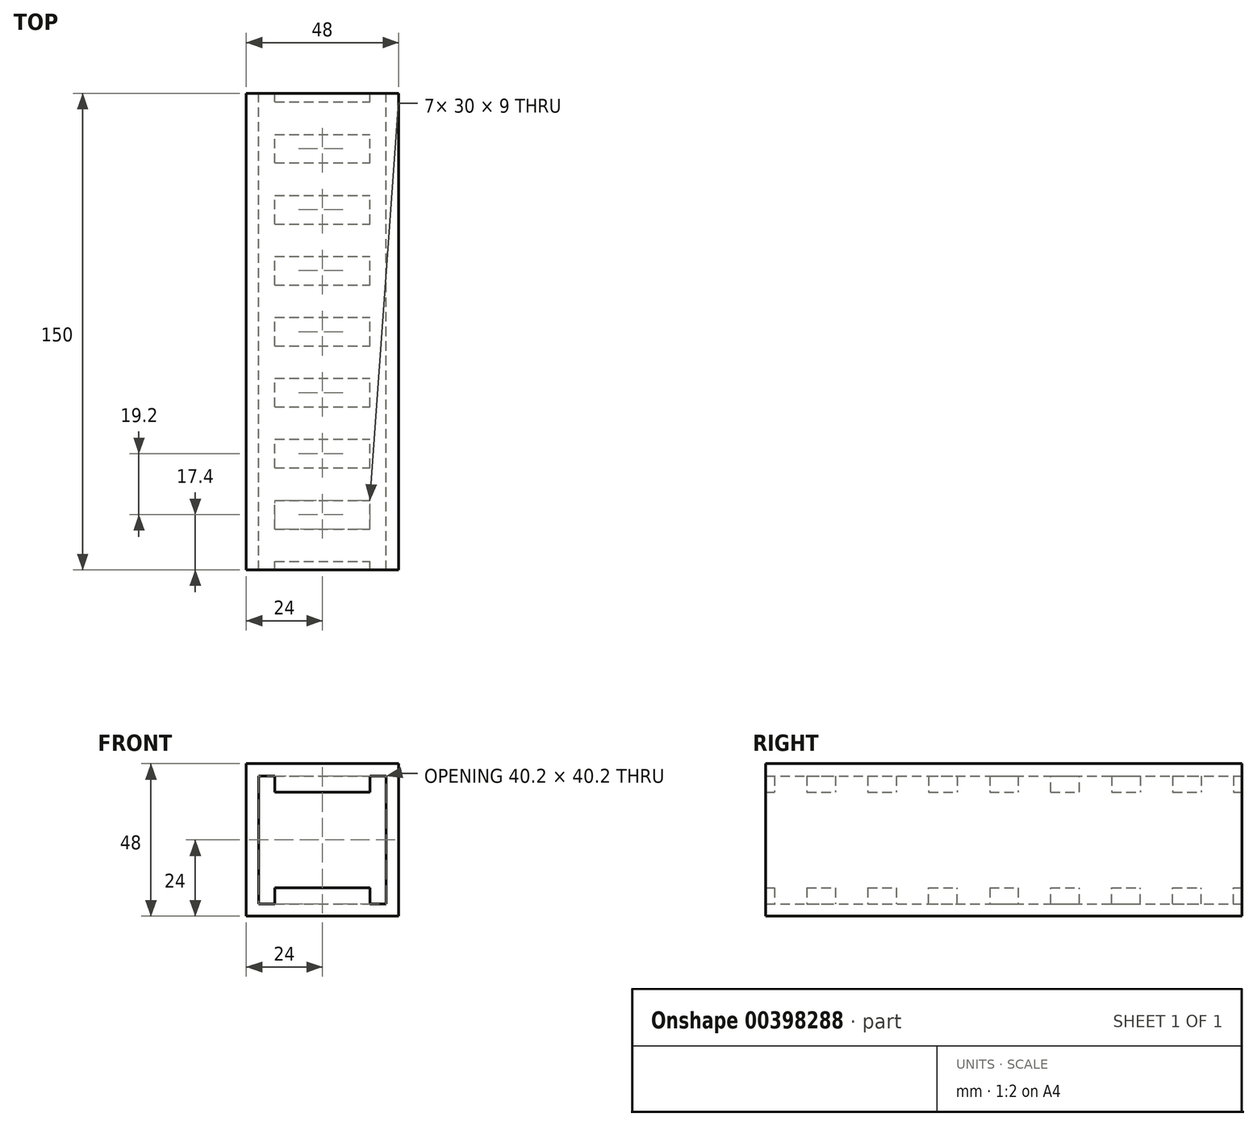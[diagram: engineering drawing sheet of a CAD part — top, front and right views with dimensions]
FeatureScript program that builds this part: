
annotation { "Feature Type Name" : "Feature", "Feature Type Description" : "" }
export const myFeature = defineFeature(function(context is Context, id is Id, definition is map)
    precondition{}
    {
        {
            var Q0;
            Q0=qCreatedBy(makeId("Front.planeOp"),FACE);
            var sketch = newSketch(context, id + "F0", { "sketchPlane" : qUnion([Q0])});
            skLineSegment(sketch, "E0.bottom", {"start": v(-24, 24) * mm, "end": v(24, 24) * mm});
            skLineSegment(sketch, "E0.top", {"start": v(-24, -24) * mm, "end": v(24, -24) * mm});
            skLineSegment(sketch, "E0.left", {"start": v(-24, 24) * mm, "end": v(-24, -24) * mm});
            skLineSegment(sketch, "E0.right", {"start": v(24, 24) * mm, "end": v(24, -24) * mm});
            skPoint(sketch, "E0.middle", {"position": v(0, 0) * mm});
            skLineSegment(sketch, "E1.bottom", {"start": v(20.1, 20.1) * mm, "end": v(-20.1, 20.1) * mm});
            skLineSegment(sketch, "E1.top", {"start": v(20.1, -20.1) * mm, "end": v(-20.1, -20.1) * mm});
            skLineSegment(sketch, "E1.left", {"start": v(20.1, 20.1) * mm, "end": v(20.1, -20.1) * mm});
            skLineSegment(sketch, "E1.right", {"start": v(-20.1, 20.1) * mm, "end": v(-20.1, -20.1) * mm});
            skSolve(sketch);
        }
        {
            var Q0;
            Q0 = qSketchRegion(id + "F0", true);
            extrude(context, id + "F1", {"entities" : qUnion([Q0]), "depth" : 150 * mm});
        }
        {
            var Q0;
            Q0=qCreatedBy(makeId("Front.planeOp"),FACE);
            var sketch = newSketch(context, id + "F2", { "sketchPlane" : qUnion([Q0])});
            skLineSegment(sketch, "E2.bottom", {"start": v(-15, 20.1) * mm, "end": v(15, 20.1) * mm});
            skLineSegment(sketch, "E2.top", {"start": v(-15, 15.1) * mm, "end": v(15, 15.1) * mm});
            skLineSegment(sketch, "E2.left", {"start": v(-15, 20.1) * mm, "end": v(-15, 15.1) * mm});
            skLineSegment(sketch, "E2.right", {"start": v(15, 20.1) * mm, "end": v(15, 15.1) * mm});
            skLineSegment(sketch, "E3.bottom", {"start": v(-15, -20.1) * mm, "end": v(15, -20.1) * mm});
            skLineSegment(sketch, "E3.top", {"start": v(-15, -15.1) * mm, "end": v(15, -15.1) * mm});
            skLineSegment(sketch, "E3.left", {"start": v(-15, -20.1) * mm, "end": v(-15, -15.1) * mm});
            skLineSegment(sketch, "E3.right", {"start": v(15, -20.1) * mm, "end": v(15, -15.1) * mm});
            skSolve(sketch);
        }
        {
            var Q0;
            Q0 = qSketchRegion(id + "F2", true);
            extrude(context, id + "F3", {"entities" : qUnion([Q0]), "operationType" : NewBodyOperationType.ADD, "depth" : 2.7 * mm});
        }
        {
            var Q0;
            Q0=qCreatedBy(makeId("Front.planeOp"),FACE);
            cPlane(context, id + "F4", {"entities" : qUnion([Q0]), "cplaneType" : CPlaneType.OFFSET, "offset" : 12.9 * mm, "width" : 150 * mm, "height" : 150 * mm});
        }
        {
            var Q0;
            Q0=qCreatedBy(id+"F4.planeOp",FACE);
            var sketch = newSketch(context, id + "F5", { "sketchPlane" : qUnion([Q0])});
            skLineSegment(sketch, "E4.bottom", {"start": v(-15, 20.1) * mm, "end": v(15, 20.1) * mm});
            skLineSegment(sketch, "E4.top", {"start": v(-15, 15.1) * mm, "end": v(15, 15.1) * mm});
            skLineSegment(sketch, "E4.left", {"start": v(-15, 20.1) * mm, "end": v(-15, 15.1) * mm});
            skLineSegment(sketch, "E4.right", {"start": v(15, 20.1) * mm, "end": v(15, 15.1) * mm});
            skLineSegment(sketch, "E5.bottom", {"start": v(-15, -20.1) * mm, "end": v(15, -20.1) * mm});
            skLineSegment(sketch, "E5.top", {"start": v(-15, -15.1) * mm, "end": v(15, -15.1) * mm});
            skLineSegment(sketch, "E5.left", {"start": v(-15, -20.1) * mm, "end": v(-15, -15.1) * mm});
            skLineSegment(sketch, "E5.right", {"start": v(15, -20.1) * mm, "end": v(15, -15.1) * mm});
            skSolve(sketch);
        }
        {
            var Q0;
            Q0 = qSketchRegion(id + "F5", true);
            extrude(context, id + "F6", {"entities" : qUnion([Q0]), "operationType" : NewBodyOperationType.ADD, "depth" : 9 * mm});
        }
        {
            var Q0;
            Q0=qCreatedBy(makeId("Front.planeOp"),FACE);
            cPlane(context, id + "F7", {"entities" : qUnion([Q0]), "cplaneType" : CPlaneType.OFFSET, "offset" : 32.1 * mm, "width" : 150 * mm, "height" : 150 * mm});
        }
        {
            var Q0;
            Q0=qCreatedBy(id+"F7.planeOp",FACE);
            var sketch = newSketch(context, id + "F8", { "sketchPlane" : qUnion([Q0])});
            skLineSegment(sketch, "E6.bottom", {"start": v(-15, 20.1) * mm, "end": v(15, 20.1) * mm});
            skLineSegment(sketch, "E6.top", {"start": v(-15, 15.1) * mm, "end": v(15, 15.1) * mm});
            skLineSegment(sketch, "E6.left", {"start": v(-15, 20.1) * mm, "end": v(-15, 15.1) * mm});
            skLineSegment(sketch, "E6.right", {"start": v(15, 20.1) * mm, "end": v(15, 15.1) * mm});
            skLineSegment(sketch, "E7.bottom", {"start": v(-15, -20.1) * mm, "end": v(15, -20.1) * mm});
            skLineSegment(sketch, "E7.top", {"start": v(-15, -15.1) * mm, "end": v(15, -15.1) * mm});
            skLineSegment(sketch, "E7.left", {"start": v(-15, -20.1) * mm, "end": v(-15, -15.1) * mm});
            skLineSegment(sketch, "E7.right", {"start": v(15, -20.1) * mm, "end": v(15, -15.1) * mm});
            skSolve(sketch);
        }
        {
            var Q0;
            Q0 = qSketchRegion(id + "F8", true);
            extrude(context, id + "F9", {"entities" : qUnion([Q0]), "operationType" : NewBodyOperationType.ADD, "depth" : 9 * mm});
        }
        {
            var Q0;
            Q0=qCreatedBy(makeId("Front.planeOp"),FACE);
            cPlane(context, id + "F10", {"entities" : qUnion([Q0]), "cplaneType" : CPlaneType.OFFSET, "offset" : 51.3 * mm, "width" : 150 * mm, "height" : 150 * mm});
        }
        {
            var Q0;
            Q0=qCreatedBy(id+"F10.planeOp",FACE);
            var sketch = newSketch(context, id + "F11", { "sketchPlane" : qUnion([Q0])});
            skLineSegment(sketch, "E8.bottom", {"start": v(-15, -20.1) * mm, "end": v(15, -20.1) * mm});
            skLineSegment(sketch, "E8.top", {"start": v(-15, -15.1) * mm, "end": v(15, -15.1) * mm});
            skLineSegment(sketch, "E8.left", {"start": v(-15, -20.1) * mm, "end": v(-15, -15.1) * mm});
            skLineSegment(sketch, "E8.right", {"start": v(15, -20.1) * mm, "end": v(15, -15.1) * mm});
            skLineSegment(sketch, "E9.bottom", {"start": v(-15, 15.1) * mm, "end": v(15, 15.1) * mm});
            skLineSegment(sketch, "E9.top", {"start": v(-15, 20.1) * mm, "end": v(15, 20.1) * mm});
            skLineSegment(sketch, "E9.left", {"start": v(-15, 15.1) * mm, "end": v(-15, 20.1) * mm});
            skLineSegment(sketch, "E9.right", {"start": v(15, 15.1) * mm, "end": v(15, 20.1) * mm});
            skSolve(sketch);
        }
        {
            var Q0;
            Q0 = qSketchRegion(id + "F11", true);
            extrude(context, id + "F12", {"entities" : qUnion([Q0]), "operationType" : NewBodyOperationType.ADD, "depth" : 9 * mm});
        }
        {
            var Q0;
            Q0=qCreatedBy(makeId("Front.planeOp"),FACE);
            cPlane(context, id + "F13", {"entities" : qUnion([Q0]), "cplaneType" : CPlaneType.OFFSET, "offset" : 70.5 * mm, "width" : 150 * mm, "height" : 150 * mm});
        }
        {
            var Q0;
            Q0=qCreatedBy(id+"F13.planeOp",FACE);
            var sketch = newSketch(context, id + "F14", { "sketchPlane" : qUnion([Q0])});
            skLineSegment(sketch, "E10.bottom", {"start": v(-15, 20.1) * mm, "end": v(15, 20.1) * mm});
            skLineSegment(sketch, "E10.top", {"start": v(-15, 15.1) * mm, "end": v(15, 15.1) * mm});
            skLineSegment(sketch, "E10.left", {"start": v(-15, 20.1) * mm, "end": v(-15, 15.1) * mm});
            skLineSegment(sketch, "E10.right", {"start": v(15, 20.1) * mm, "end": v(15, 15.1) * mm});
            skLineSegment(sketch, "E11.bottom", {"start": v(-15, -15.1) * mm, "end": v(15, -15.1) * mm});
            skLineSegment(sketch, "E11.top", {"start": v(-15, -20.1) * mm, "end": v(15, -20.1) * mm});
            skLineSegment(sketch, "E11.left", {"start": v(-15, -15.1) * mm, "end": v(-15, -20.1) * mm});
            skLineSegment(sketch, "E11.right", {"start": v(15, -15.1) * mm, "end": v(15, -20.1) * mm});
            skSolve(sketch);
        }
        {
            var Q0;
            Q0 = qSketchRegion(id + "F14", true);
            extrude(context, id + "F15", {"entities" : qUnion([Q0]), "operationType" : NewBodyOperationType.ADD, "depth" : 9 * mm});
        }
        {
            var Q0;
            Q0=qCreatedBy(makeId("Front.planeOp"),FACE);
            cPlane(context, id + "F16", {"entities" : qUnion([Q0]), "cplaneType" : CPlaneType.OFFSET, "offset" : 89.7 * mm, "width" : 150 * mm, "height" : 150 * mm});
        }
        {
            var Q0;
            Q0=qCreatedBy(id+"F16.planeOp",FACE);
            var sketch = newSketch(context, id + "F17", { "sketchPlane" : qUnion([Q0])});
            skLineSegment(sketch, "E12.bottom", {"start": v(-15, 20.1) * mm, "end": v(15, 20.1) * mm});
            skLineSegment(sketch, "E12.top", {"start": v(-15, 15.1) * mm, "end": v(15, 15.1) * mm});
            skLineSegment(sketch, "E12.left", {"start": v(-15, 20.1) * mm, "end": v(-15, 15.1) * mm});
            skLineSegment(sketch, "E12.right", {"start": v(15, 20.1) * mm, "end": v(15, 15.1) * mm});
            skLineSegment(sketch, "E13.bottom", {"start": v(-15, -20.1) * mm, "end": v(15, -20.1) * mm});
            skLineSegment(sketch, "E13.top", {"start": v(-15, -15.1) * mm, "end": v(15, -15.1) * mm});
            skLineSegment(sketch, "E13.left", {"start": v(-15, -20.1) * mm, "end": v(-15, -15.1) * mm});
            skLineSegment(sketch, "E13.right", {"start": v(15, -20.1) * mm, "end": v(15, -15.1) * mm});
            skSolve(sketch);
        }
        {
            var Q0;
            Q0 = qSketchRegion(id + "F17", true);
            extrude(context, id + "F18", {"entities" : qUnion([Q0]), "operationType" : NewBodyOperationType.ADD, "depth" : 9 * mm});
        }
        {
            var Q0;
            Q0=qCreatedBy(makeId("Front.planeOp"),FACE);
            cPlane(context, id + "F19", {"entities" : qUnion([Q0]), "cplaneType" : CPlaneType.OFFSET, "offset" : 108.9 * mm, "width" : 150 * mm, "height" : 150 * mm});
        }
        {
            var Q0;
            Q0=qCreatedBy(id+"F19.planeOp",FACE);
            var sketch = newSketch(context, id + "F20", { "sketchPlane" : qUnion([Q0])});
            skLineSegment(sketch, "E14.bottom", {"start": v(-15, 20.1) * mm, "end": v(15, 20.1) * mm});
            skLineSegment(sketch, "E14.top", {"start": v(-15, 15.1) * mm, "end": v(15, 15.1) * mm});
            skLineSegment(sketch, "E14.left", {"start": v(-15, 20.1) * mm, "end": v(-15, 15.1) * mm});
            skLineSegment(sketch, "E14.right", {"start": v(15, 20.1) * mm, "end": v(15, 15.1) * mm});
            skLineSegment(sketch, "E15.bottom", {"start": v(-15, -15.1) * mm, "end": v(15, -15.1) * mm});
            skLineSegment(sketch, "E15.top", {"start": v(-15, -20.1) * mm, "end": v(15, -20.1) * mm});
            skLineSegment(sketch, "E15.left", {"start": v(-15, -15.1) * mm, "end": v(-15, -20.1) * mm});
            skLineSegment(sketch, "E15.right", {"start": v(15, -15.1) * mm, "end": v(15, -20.1) * mm});
            skSolve(sketch);
        }
        {
            var Q0;
            Q0 = qSketchRegion(id + "F20", true);
            extrude(context, id + "F21", {"entities" : qUnion([Q0]), "operationType" : NewBodyOperationType.ADD, "depth" : 9 * mm});
        }
        {
            var Q0;
            Q0=qCreatedBy(makeId("Front.planeOp"),FACE);
            cPlane(context, id + "F22", {"entities" : qUnion([Q0]), "cplaneType" : CPlaneType.OFFSET, "offset" : 128.1 * mm, "width" : 150 * mm, "height" : 150 * mm});
        }
        {
            var Q0;
            Q0=qCreatedBy(id+"F22.planeOp",FACE);
            var sketch = newSketch(context, id + "F23", { "sketchPlane" : qUnion([Q0])});
            skLineSegment(sketch, "E16.bottom", {"start": v(-15, 20.1) * mm, "end": v(15, 20.1) * mm});
            skLineSegment(sketch, "E16.top", {"start": v(-15, 15.1) * mm, "end": v(15, 15.1) * mm});
            skLineSegment(sketch, "E16.left", {"start": v(-15, 20.1) * mm, "end": v(-15, 15.1) * mm});
            skLineSegment(sketch, "E16.right", {"start": v(15, 20.1) * mm, "end": v(15, 15.1) * mm});
            skLineSegment(sketch, "E17.bottom", {"start": v(-15, -15.1) * mm, "end": v(15, -15.1) * mm});
            skLineSegment(sketch, "E17.top", {"start": v(-15, -20.1) * mm, "end": v(15, -20.1) * mm});
            skLineSegment(sketch, "E17.left", {"start": v(-15, -15.1) * mm, "end": v(-15, -20.1) * mm});
            skLineSegment(sketch, "E17.right", {"start": v(15, -15.1) * mm, "end": v(15, -20.1) * mm});
            skSolve(sketch);
        }
        {
            var Q0;
            Q0 = qSketchRegion(id + "F23", true);
            extrude(context, id + "F24", {"entities" : qUnion([Q0]), "operationType" : NewBodyOperationType.ADD, "depth" : 9 * mm});
        }
        {
            var Q0;
            Q0=qCreatedBy(makeId("Front.planeOp"),FACE);
            cPlane(context, id + "F25", {"entities" : qUnion([Q0]), "cplaneType" : CPlaneType.OFFSET, "offset" : 147.3 * mm, "width" : 150 * mm, "height" : 150 * mm});
        }
        {
            var Q0;
            Q0=qCreatedBy(id+"F25.planeOp",FACE);
            var sketch = newSketch(context, id + "F26", { "sketchPlane" : qUnion([Q0])});
            skLineSegment(sketch, "E18.bottom", {"start": v(-15, 20.1) * mm, "end": v(15, 20.1) * mm});
            skLineSegment(sketch, "E18.top", {"start": v(-15, 15.1) * mm, "end": v(15, 15.1) * mm});
            skLineSegment(sketch, "E18.left", {"start": v(-15, 20.1) * mm, "end": v(-15, 15.1) * mm});
            skLineSegment(sketch, "E18.right", {"start": v(15, 20.1) * mm, "end": v(15, 15.1) * mm});
            skLineSegment(sketch, "E19.bottom", {"start": v(-15, -15.1) * mm, "end": v(15, -15.1) * mm});
            skLineSegment(sketch, "E19.top", {"start": v(-15, -20.1) * mm, "end": v(15, -20.1) * mm});
            skLineSegment(sketch, "E19.left", {"start": v(-15, -15.1) * mm, "end": v(-15, -20.1) * mm});
            skLineSegment(sketch, "E19.right", {"start": v(15, -15.1) * mm, "end": v(15, -20.1) * mm});
            skSolve(sketch);
        }
        {
            var Q0;
            Q0 = qSketchRegion(id + "F26", true);
            extrude(context, id + "F27", {"entities" : qUnion([Q0]), "operationType" : NewBodyOperationType.ADD, "depth" : 2.7 * mm});
        }
    });
